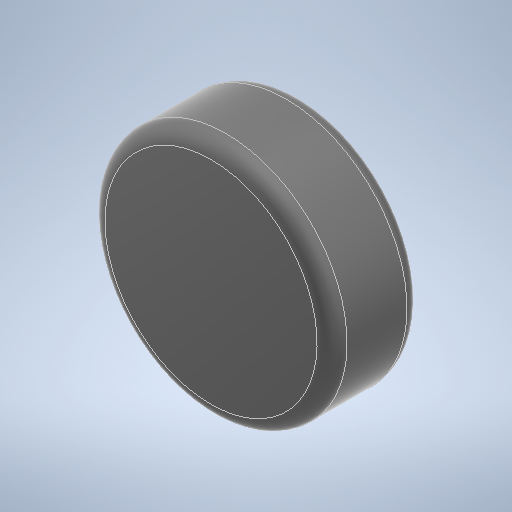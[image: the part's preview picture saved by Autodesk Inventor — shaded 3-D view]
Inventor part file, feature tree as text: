
AUTODESK INVENTOR PART (.ipt)
format: ipt  version: 2025.1 (Build 291241020, 241B)  size: 441,856 bytes
history: native  units: mm
features: revolve x1, fillet x1, sketch x1
ambient origin geometry x8: Origin, YZ Plane, XZ Plane, XY Plane, X Axis, Y Axis, Z Axis, Center Point
bodies: Solid1 (feature_tree)
feature tree (3):
  revolve  "Revolution1"  [1 undecoded]
  fillet  "Fillet1"  Radius=12.0mm
  sketch  "Sketch1"  dims[d0=16.15mm d1=10.2mm d2=12.0mm d3=5.0mm d4=360.0deg d5=2.0mm]
note: 1 required parameter value undecoded (feature->parameter linkage not recoverable at this tier; creation-order binding heuristic only, values carry confidence <= 0.55)
